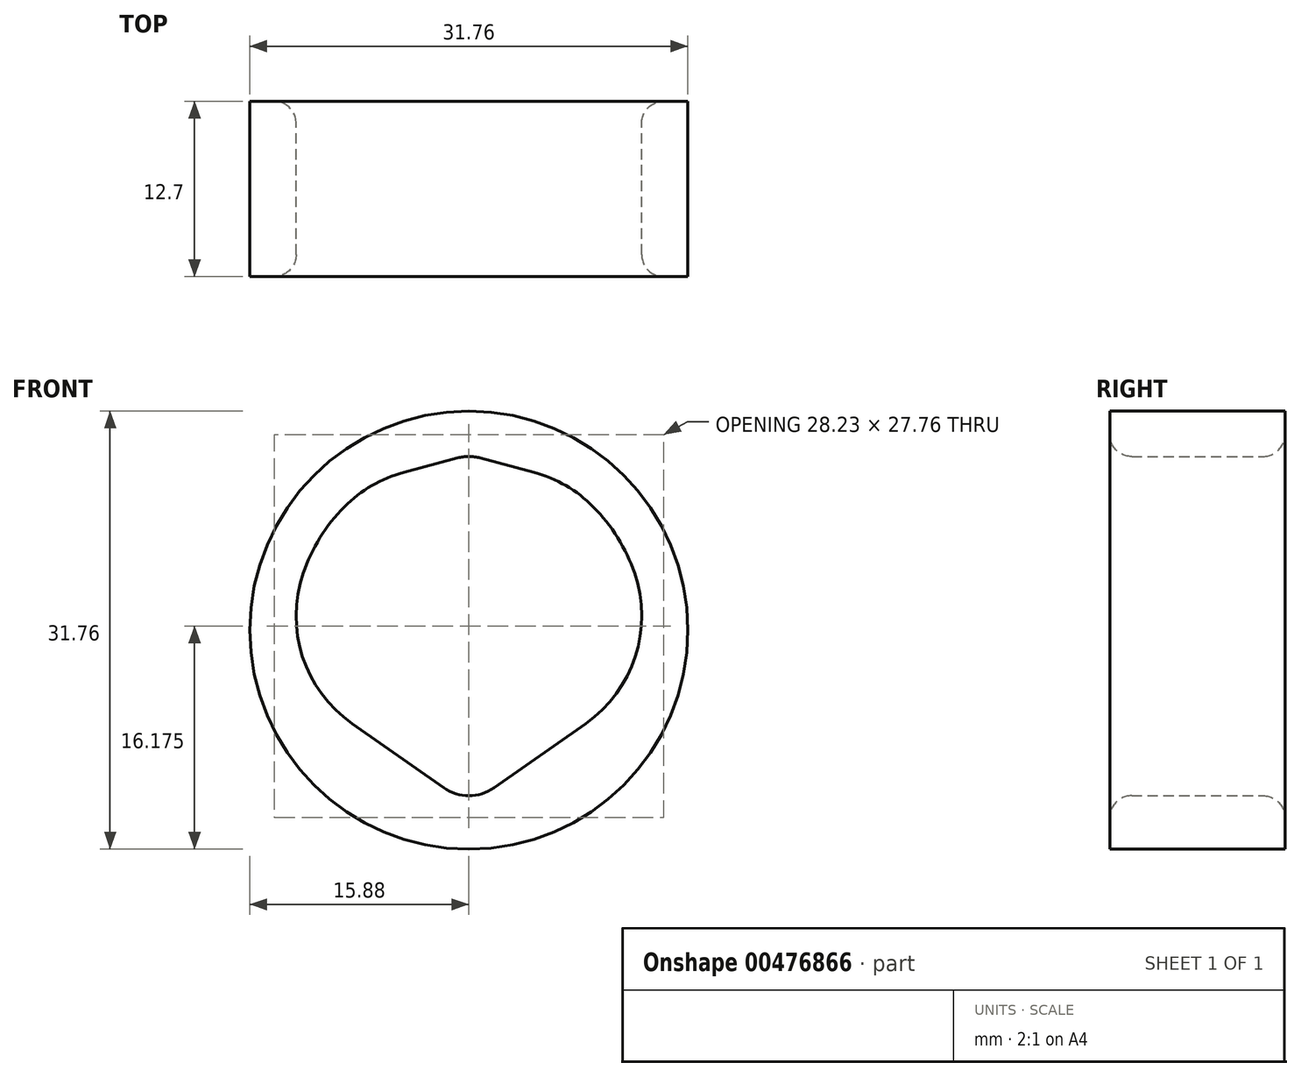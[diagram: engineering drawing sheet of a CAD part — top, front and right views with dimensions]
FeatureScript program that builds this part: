
annotation { "Feature Type Name" : "Feature", "Feature Type Description" : "" }
export const myFeature = defineFeature(function(context is Context, id is Id, definition is map)
    precondition{}
    {
        {
            var Q0;
            Q0=qCreatedBy(makeId("Front.planeOp"),FACE);
            var sketch = newSketch(context, id + "F0", { "sketchPlane" : qUnion([Q0])});
            skArc(sketch, "E0", {"start": v(-6.35, 11) * mm, "mid": v(-11.93, 4.34) * mm, "end": v(-11.93, -4.34) * mm});
            skCircle(sketch, "E1", {"center": v(0, 0) * mm, "radius": 15.88 * mm});
            skLineSegment(sketch, "E2", {"start": v(0, -12.7) * mm, "end": v(-11.93, -4.34) * mm});
            skLineSegment(sketch, "E3", {"start": v(0, 12.7) * mm, "end": v(-6.35, 11) * mm});
            skLineSegment(sketch, "E4.MirrorCS", {"start": v(0, 12.7) * mm, "end": v(6.35, 11) * mm});
            skLineSegment(sketch, "E5.MirrorCS", {"start": v(0, -12.7) * mm, "end": v(11.93, -4.34) * mm});
            skArc(sketch, "E6.trimOffspring", {"start": v(11.93, -4.34) * mm, "mid": v(11.93, 4.34) * mm, "end": v(6.35, 11) * mm});
            skSolve(sketch);
        }
        {
            var Q0;
            Q0=makeQuery(id+"F0.imprint","IMPRINT",FACE,{"disambiguationData":[TD([[makeQuery(id+"F0.imprint","IMPRINT",EDGE,{"derivedFrom":sQuery(id+"F0.wireOp",EDGE,"E0")}),-1.0]])]});
            extrude(context, id + "F1", {"entities" : qUnion([Q0]), "endBound" : BoundingType.SYMMETRIC, "depth" : 12.7 * mm});
        }
        {
            var Q0;
            Q0=makeQuery(id+"F1.opExtrude","SWEPT_EDGE",EDGE,{"disambiguationData":[OSD([sQuery(id+"F0.wireOp",EDGE,"E0"),sQuery(id+"F0.wireOp",EDGE,"E2")])]});
            var Q1;
            Q1=makeQuery(id+"F1.opExtrude","SWEPT_EDGE",EDGE,{"disambiguationData":[OSD([sQuery(id+"F0.wireOp",EDGE,"E5.MirrorCS"),sQuery(id+"F0.wireOp",EDGE,"E6.trimOffspring")])]});
            var Q2;
            Q2=makeQuery(id+"F1.opExtrude","SWEPT_EDGE",EDGE,{"disambiguationData":[OSD([sQuery(id+"F0.wireOp",EDGE,"E0"),sQuery(id+"F0.wireOp",EDGE,"E3")])]});
            var Q3;
            Q3=makeQuery(id+"F1.opExtrude","SWEPT_EDGE",EDGE,{"disambiguationData":[OSD([sQuery(id+"F0.wireOp",EDGE,"E4.MirrorCS"),sQuery(id+"F0.wireOp",EDGE,"E6.trimOffspring")])]});
            fillet(context, id + "F2", {"entities" : qUnion([Q0, Q1, Q2, Q3]), "radius" : 9.52 * mm, "tangentPropagation" : true, "allowEdgeOverflow" : false});
        }
        {
            var Q0;
            Q0=makeQuery(id+"F1.opExtrude","SWEPT_EDGE",EDGE,{"disambiguationData":[OSD([sQuery(id+"F0.wireOp",EDGE,"E2"),sQuery(id+"F0.wireOp",EDGE,"E5.MirrorCS")])]});
            var Q1;
            Q1=makeQuery(id+"F1.opExtrude","SWEPT_EDGE",EDGE,{"disambiguationData":[OSD([sQuery(id+"F0.wireOp",EDGE,"E3"),sQuery(id+"F0.wireOp",EDGE,"E4.MirrorCS")])]});
            fillet(context, id + "F3", {"entities" : qUnion([Q0, Q1]), "radius" : 3.17 * mm, "tangentPropagation" : true, "allowEdgeOverflow" : false});
        }
        {
            var Q0;
            Q0=makeQuery(id+"F1.opExtrude","CAP_EDGE",EDGE,{"disambiguationData":[OSD([sQuery(id+"F0.wireOp",EDGE,"E4.MirrorCS")])],"isStart":false});
            var Q1;
            Q1=makeQuery(id+"F1.opExtrude","CAP_EDGE",EDGE,{"disambiguationData":[OSD([sQuery(id+"F0.wireOp",EDGE,"E4.MirrorCS")])],"isStart":true});
            var Q2;
            {var subQ0=sQuery(id+"F0.wireOp",EDGE,"E5.MirrorCS");var subQ1=sQuery(id+"F0.wireOp",EDGE,"E2");Q2=makeQuery(id+"F3.opFillet","BLEND_EDGE",EDGE,{"blendedFrom":[makeQuery(id+"F1.opExtrude","SWEPT_EDGE",EDGE,{"disambiguationData":[OSD([subQ1,subQ0])]}),makeQuery(id+"F1.opExtrude","CAP_FACE",FACE,{"disambiguationData":[OSD([sQuery(id+"F0.wireOp",EDGE,"E0"),sQuery(id+"F0.wireOp",EDGE,"E1"),subQ1,sQuery(id+"F0.wireOp",EDGE,"E3"),sQuery(id+"F0.wireOp",EDGE,"E4.MirrorCS"),subQ0,sQuery(id+"F0.wireOp",EDGE,"E6.trimOffspring")])],"isStart":false})],"blendedInto":[makeQuery(id+"F1.opExtrude","CAP_FACE",FACE,{"disambiguationData":[OSD([sQuery(id+"F0.wireOp",EDGE,"E0"),sQuery(id+"F0.wireOp",EDGE,"E1"),subQ1,sQuery(id+"F0.wireOp",EDGE,"E3"),sQuery(id+"F0.wireOp",EDGE,"E4.MirrorCS"),subQ0,sQuery(id+"F0.wireOp",EDGE,"E6.trimOffspring")])],"isStart":false})]});}
            var Q3;
            {var subQ0=sQuery(id+"F0.wireOp",EDGE,"E5.MirrorCS");var subQ1=sQuery(id+"F0.wireOp",EDGE,"E2");Q3=makeQuery(id+"F3.opFillet","BLEND_EDGE",EDGE,{"blendedFrom":[makeQuery(id+"F1.opExtrude","SWEPT_EDGE",EDGE,{"disambiguationData":[OSD([subQ1,subQ0])]}),makeQuery(id+"F1.opExtrude","CAP_FACE",FACE,{"disambiguationData":[OSD([sQuery(id+"F0.wireOp",EDGE,"E0"),sQuery(id+"F0.wireOp",EDGE,"E1"),subQ1,sQuery(id+"F0.wireOp",EDGE,"E3"),sQuery(id+"F0.wireOp",EDGE,"E4.MirrorCS"),subQ0,sQuery(id+"F0.wireOp",EDGE,"E6.trimOffspring")])],"isStart":true})],"blendedInto":[makeQuery(id+"F1.opExtrude","CAP_FACE",FACE,{"disambiguationData":[OSD([sQuery(id+"F0.wireOp",EDGE,"E0"),sQuery(id+"F0.wireOp",EDGE,"E1"),subQ1,sQuery(id+"F0.wireOp",EDGE,"E3"),sQuery(id+"F0.wireOp",EDGE,"E4.MirrorCS"),subQ0,sQuery(id+"F0.wireOp",EDGE,"E6.trimOffspring")])],"isStart":true})]});}
            fillet(context, id + "F4", {"entities" : qUnion([Q0, Q1, Q2, Q3]), "radius" : 1.59 * mm, "tangentPropagation" : true, "allowEdgeOverflow" : false});
        }
    });
